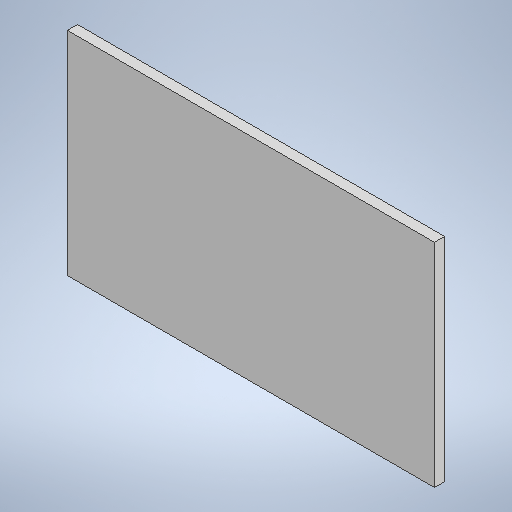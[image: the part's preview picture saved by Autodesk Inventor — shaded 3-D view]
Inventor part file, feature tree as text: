
AUTODESK INVENTOR PART (.ipt)
format: ipt  version: 2025.1 (Build 291241000, 241)  size: 182,784 bytes
history: native  units: in
note: dims shown in document units (in); Inventor stores cm internally (conversion verified against a paired STEP export)
features: extrude x1, sketch x1
ambient origin geometry x8: Origin, YZ Plane, XZ Plane, XY Plane, X Axis, Y Axis, Z Axis, Center Point
bodies: Solid1 (feature_tree)
feature tree (2):
  extrude  "Extrusion1"  Depth=1.047in
  sketch  "Sketch1"  dims[d0=1.81in d1=1.047in d2=0.05in d3=0.0in]
